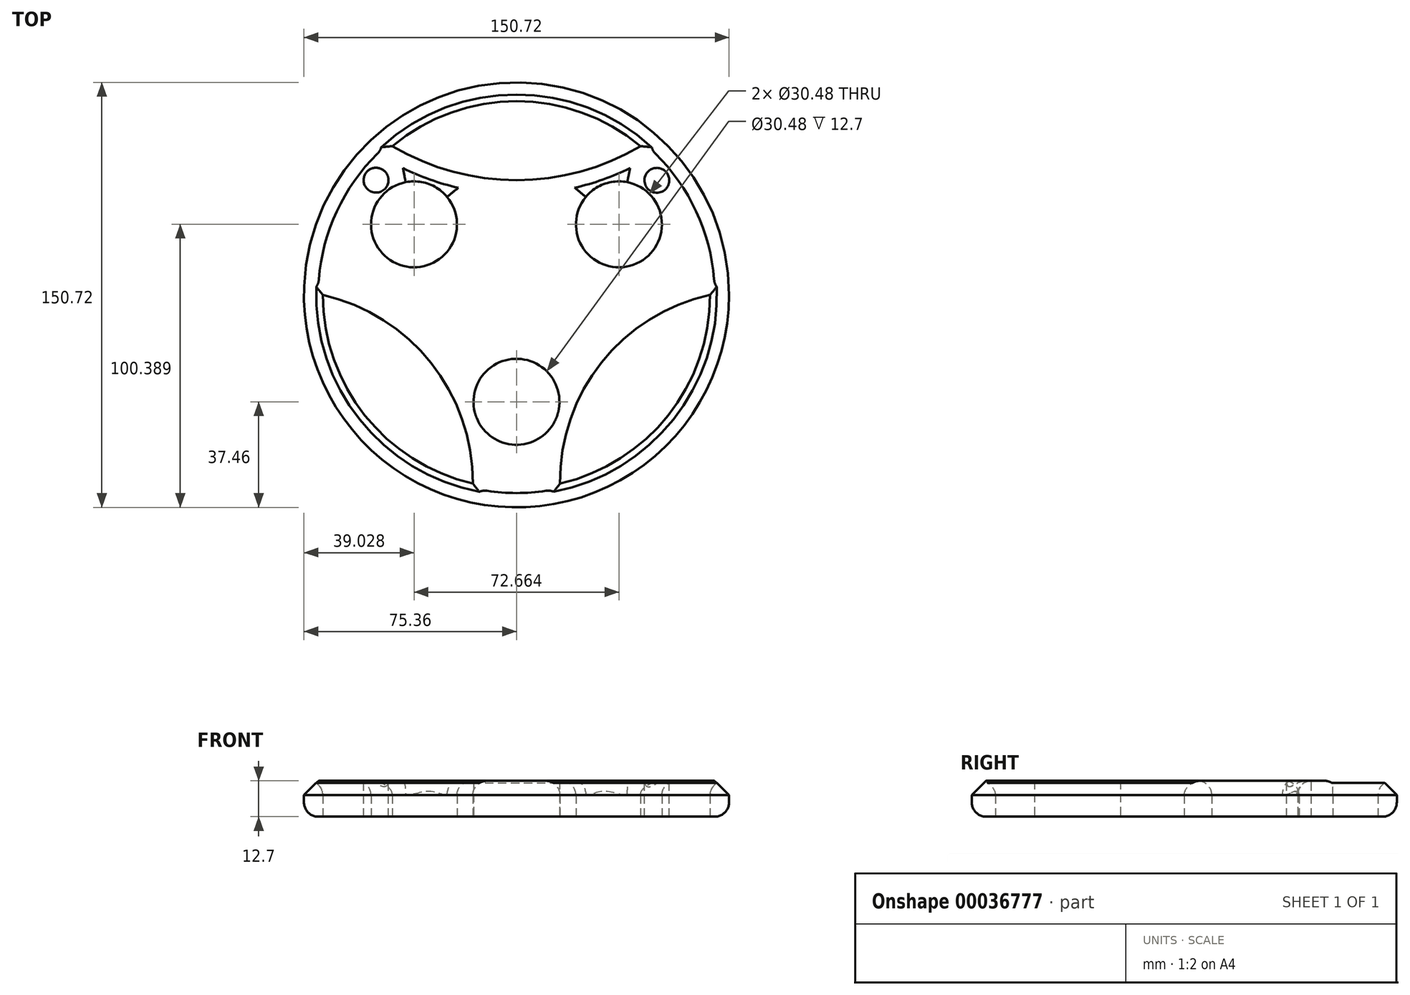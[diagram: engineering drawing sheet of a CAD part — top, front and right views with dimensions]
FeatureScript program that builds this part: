
annotation { "Feature Type Name" : "Feature", "Feature Type Description" : "" }
export const myFeature = defineFeature(function(context is Context, id is Id, definition is map)
    precondition{}
    {
        {
            var Q0;
            Q0=qCreatedBy(makeId("Top.planeOp"),FACE);
            var sketch = newSketch(context, id + "F0", { "sketchPlane" : qUnion([Q0])});
            skCircle(sketch, "E0", {"center": v(0, 0) * mm, "radius": 75.36 * mm});
            skCircle(sketch, "E1", {"center": v(0, 0) * mm, "radius": 68.68 * mm});
            skArc(sketch, "E2", {"start": v(68.68, 0) * mm, "mid": v(29.6, -24.67) * mm, "end": v(15.5, -68.68) * mm});
            skLineSegment(sketch, "E3", {"start": v(-43.99, 52.74) * mm, "end": v(43.99, 52.74) * mm});
            skArc(sketch, "E4", {"start": v(-43.99, 52.74) * mm, "mid": v(0, 40.7) * mm, "end": v(43.99, 52.74) * mm});
            skArc(sketch, "E5", {"start": v(-15.5, -68.68) * mm, "mid": v(-29.77, -24.8) * mm, "end": v(-68.68, 0) * mm});
            skCircle(sketch, "E6", {"center": v(-36.33, 25.03) * mm, "radius": 15.24 * mm});
            skCircle(sketch, "E7", {"center": v(36.33, 25.03) * mm, "radius": 15.24 * mm});
            skCircle(sketch, "E8", {"center": v(0, -37.9) * mm, "radius": 15.24 * mm});
            skLineSegment(sketch, "E9", {"start": v(-68.68, 0) * mm, "end": v(68.68, 0) * mm});
            skSolve(sketch);
        }
        {
            var Q0;
            Q0=makeQuery(id+"F0.imprint","IMPRINT",FACE,{"disambiguationData":[TD([[makeQuery(id+"F0.imprint","IMPRINT",EDGE,{"derivedFrom":sQuery(id+"F0.wireOp",EDGE,"E0")}),1.0]])]});
            var Q1;
            {var subQ1=sQuery(id+"F0.wireOp",EDGE,"E4");Q1=makeQuery(id+"F0.imprint","IMPRINT",FACE,{"disambiguationData":[TD([[makeQuery(id+"F0.imprint","IMPRINT",EDGE,{"derivedFrom":subQ1}),-1.0]])]});}
            var Q2;
            Q2=makeQuery(id+"F0.imprint","IMPRINT",FACE,{"disambiguationData":[TD([[makeQuery(id+"F0.imprint","IMPRINT",EDGE,{"derivedFrom":sQuery(id+"F0.wireOp",EDGE,"E8")}),-1.0]])]});
            extrude(context, id + "F1", {"entities" : qUnion([Q0, Q1, Q2]), "depth" : 12.7 * mm});
        }
        {
            var Q0;
            Q0=makeQuery(id+"F1.opExtrude","CAP_FACE",FACE,{"disambiguationData":[OSD([sQuery(id+"F0.wireOp",EDGE,"E0"),sQuery(id+"F0.wireOp",EDGE,"E1"),sQuery(id+"F0.wireOp",EDGE,"E2"),sQuery(id+"F0.wireOp",EDGE,"E4"),sQuery(id+"F0.wireOp",EDGE,"E5"),sQuery(id+"F0.wireOp",EDGE,"E6"),sQuery(id+"F0.wireOp",EDGE,"E7"),sQuery(id+"F0.wireOp",EDGE,"E8")])],"isStart":false});
            var sketch = newSketch(context, id + "F2", { "sketchPlane" : qUnion([Q0])});
            skCircle(sketch, "E10", {"center": v(-49.79, 40.7) * mm, "radius": 4.4 * mm});
            skCircle(sketch, "E11", {"center": v(49.79, 40.64) * mm, "radius": 4.4 * mm});
            skSolve(sketch);
        }
        {
            var Q0;
            Q0 = qSketchRegion(id + "F2", true);
            extrude(context, id + "F3", {"entities" : qUnion([Q0]), "operationType" : NewBodyOperationType.REMOVE, "oppositeDirection" : true, "depth" : 25.4 * mm});
        }
        {
            var Q0;
            Q0=makeQuery(id+"F1.opExtrude","CAP_EDGE",EDGE,{"disambiguationData":[OSD([sQuery(id+"F0.wireOp",EDGE,"E5")])],"isStart":false});
            var Q1;
            {var subQ0=sQuery(id+"F0.wireOp",EDGE,"E1");var subQ1=sQuery(id+"F0.wireOp",EDGE,"E5");Q1=makeQuery(id+"F1.opExtrude","CAP_EDGE",EDGE,{"disambiguationData":[OSD([subQ0]),TDD([makeQuery(id+"F0.imprint","IMPRINT",EDGE,{"disambiguationData":[TD([[makeQuery(id+"F0.imprint","INTERSECT",VERTEX,{"derivedFrom":[subQ0,subQ1]}),1.0]])],"derivedFrom":subQ0})])],"isStart":false});}
            var Q2;
            Q2=makeQuery(id+"F1.opExtrude","CAP_EDGE",EDGE,{"disambiguationData":[OSD([sQuery(id+"F0.wireOp",EDGE,"E2")])],"isStart":false});
            var Q3;
            {var subQ0=sQuery(id+"F0.wireOp",EDGE,"E1");var subQ1=sQuery(id+"F0.wireOp",EDGE,"E2");Q3=makeQuery(id+"F1.opExtrude","CAP_EDGE",EDGE,{"disambiguationData":[OSD([subQ0]),TDD([makeQuery(id+"F0.imprint","IMPRINT",EDGE,{"disambiguationData":[TD([[makeQuery(id+"F0.imprint","INTERSECT",VERTEX,{"derivedFrom":[subQ0,subQ1]}),-1.0]])],"derivedFrom":subQ0})])],"isStart":false});}
            var Q4;
            Q4=makeQuery(id+"F1.opExtrude","CAP_EDGE",EDGE,{"disambiguationData":[OSD([sQuery(id+"F0.wireOp",EDGE,"E4")])],"isStart":false});
            var Q5;
            {var subQ0=sQuery(id+"F0.wireOp",EDGE,"E1");var subQ1=sQuery(id+"F0.wireOp",EDGE,"E3");var subQ2=sQuery(id+"F0.wireOp",EDGE,"E4");Q5=makeQuery(id+"F1.opExtrude","CAP_EDGE",EDGE,{"disambiguationData":[OSD([subQ0]),TDD([makeQuery(id+"F0.imprint","IMPRINT",EDGE,{"disambiguationData":[TD([[makeQuery(id+"F0.imprint","INTERSECT",VERTEX,{"disambiguationData":[OD(0.0)],"derivedFrom":[subQ0,subQ1,subQ2]}),1.0]])],"derivedFrom":subQ0})])],"isStart":false});}
            fillet(context, id + "F4", {"entities" : qUnion([Q0, Q1, Q2, Q3, Q4, Q5]), "radius" : 5.08 * mm, "tangentPropagation" : true, "allowEdgeOverflow" : false});
        }
        {
            var Q0;
            Q0=makeQuery(id+"F1.opExtrude","CAP_EDGE",EDGE,{"disambiguationData":[OSD([sQuery(id+"F0.wireOp",EDGE,"E0")])],"isStart":false});
            chamfer(context, id + "F5", {"entities" : qUnion([Q0]), "width" : 5.08 * mm, "tangentPropagation" : true});
        }
        {
            var Q0;
            Q0=makeQuery(id+"F1.opExtrude","CAP_EDGE",EDGE,{"disambiguationData":[OSD([sQuery(id+"F0.wireOp",EDGE,"E6")])],"isStart":false});
            var Q1;
            Q1=makeQuery(id+"F1.opExtrude","CAP_EDGE",EDGE,{"disambiguationData":[OSD([sQuery(id+"F0.wireOp",EDGE,"E7")])],"isStart":false});
            fillet(context, id + "F6", {"entities" : qUnion([Q0, Q1]), "radius" : 5.08 * mm, "tangentPropagation" : true, "allowEdgeOverflow" : false});
        }
        {
            var Q0;
            Q0=makeQuery(id+"F1.opExtrude","CAP_EDGE",EDGE,{"disambiguationData":[OSD([sQuery(id+"F0.wireOp",EDGE,"E0")])],"isStart":true});
            fillet(context, id + "F7", {"entities" : qUnion([Q0]), "radius" : 5.08 * mm, "tangentPropagation" : true, "allowEdgeOverflow" : false});
        }
    });
